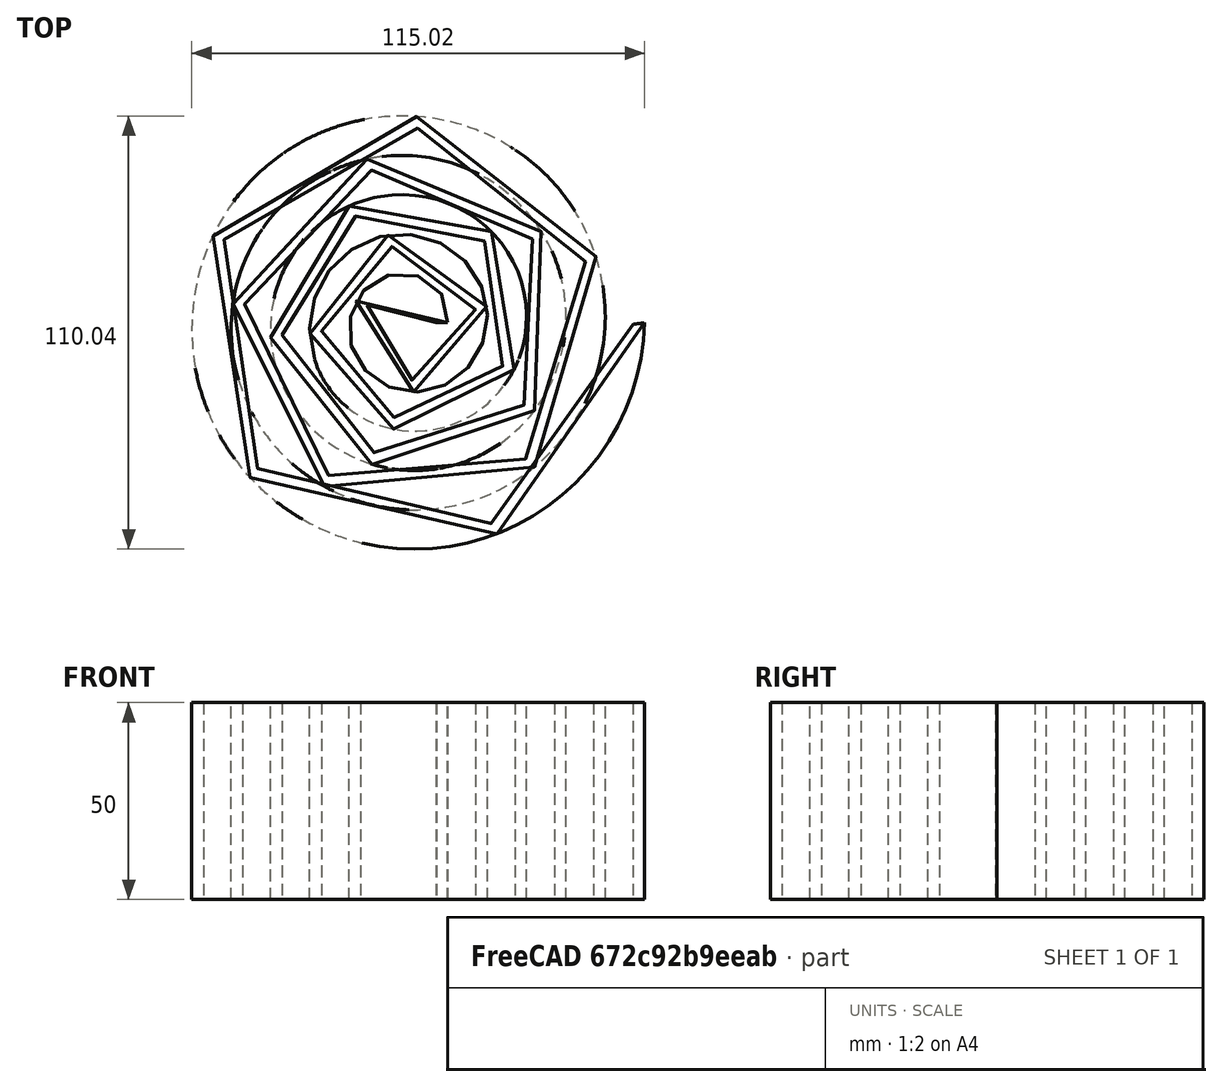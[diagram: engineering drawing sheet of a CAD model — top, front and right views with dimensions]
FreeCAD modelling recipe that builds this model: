
FCSTD DOCUMENT  (FreeCAD 0.17R13247 (Git))
Label: MOLA ESPIRAL
License: All rights reserved
LicenseURL: http://en.wikipedia.org/wiki/All_rights_reserved
objects: Part::Spiral×1, Sketcher::SketchObject×1, PartDesign::Body×1, Part::Sweep×1, Fem::FemSolverObjectPython×1, App::MaterialObjectPython×1, Fem::ConstraintFixed×1, Fem::ConstraintForce×1, Fem::FemMeshShapeNetgenObject×1, Fem::FemMeshObjectPython×1, Fem::FemResultObjectPython×1, Fem::FemAnalysis×1
note: 4 computed .brp shape members not serialized (recipe doc carries the construction recipe); baked Part::Feature solids carry a one-line shape summary decoded from their .brp

FEATURE [Part::Spiral] Spiral
  AttacherType = Attacher::AttachEngine3D
  Growth = 10
  Radius = 10
  Rotations = 5
FEATURE [Sketcher::SketchObject] Sketch
  AttachmentOffset = pos=(10,0,0) rot=(0,0,1;0rad)
  MapMode = 5
  Placement = pos=(10,0,0) rot=(1,0,0;1.5708rad)
  Support = -> [XZ_Plane]
  sketch-geometry (4):
    g0: LineSegment StartX=-3 StartY=0 StartZ=0 EndX=0 EndY=0 EndZ=0
    g1: LineSegment StartX=0 StartY=0 StartZ=0 EndX=0 EndY=50 EndZ=0
    g2: LineSegment StartX=0 StartY=50 StartZ=0 EndX=-3 EndY=50 EndZ=0
    g3: LineSegment StartX=-3 StartY=50 StartZ=0 EndX=-3 EndY=0 EndZ=0
  constraints (12):
    c: Coincident(g0,g1)
    c: Coincident(g1,g2)
    c: Coincident(g2,g3)
    c: Coincident(g3,g0)
    c: Horizontal(g0)
    c: Horizontal(g2)
    c: Vertical(g1)
    c: Vertical(g3)
    c: PointOnObject(g0,g-1)
    c: DistanceX(g2,g2) = 3
    c: DistanceY(g3,g3) = 50
    c: Coincident(g0,g-1)
FEATURE [PartDesign::Body] Body
  Group = -> [Sketch]
  Origin = -> Origin
FEATURE [Part::Sweep] Sweep
  Frenet = true
  Sections = -> [Sketch]
  Solid = true
  Spine = -> Spiral [Edge1]
  Transition = 1
FEATURE [Fem::FemSolverObjectPython] CalculiXccxTools  # FEM object (typed FeaturePython)
  AnalysisType = 0
  BeamShellResultOutput3D = false
  EigenmodeHighLimit = 1000000
  EigenmodeLowLimit = 0
  EigenmodesCount = 10
  GeometricalNonlinearity = 0
  IterationsControlParameterCutb = 0.25,0.5,0.75,0.85,,,1.5,
  IterationsControlParameterIter = 4,8,9,200,10,400,,200,,
  IterationsControlParameterTimeUse = false
  IterationsThermoMechMaximum = 2000
  IterationsUserDefinedIncrementations = false
  IterationsUserDefinedTimeStepLength = false
  MaterialNonlinearity = 0
  MatrixSolverType = 0
  SplitInputWriter = false
  ThermoMechSteadyState = true
  TimeEnd = 1
  TimeInitialStep = 0.01
FEATURE [App::MaterialObjectPython] SolidMaterial  # material (typed FeaturePython)
  Category = 0
  Material = Density=7900.0 kg/m^3,+10 more (map truncated)
FEATURE [Fem::ConstraintFixed] FemConstraintFixed
  NormalDirection = (0,-1,0)
  Normals = (12) [(8.7142e-16,-1,1.60878e-16),(8.7142e-16,-1,1.60878e-16),(8.7142e-16,-1,1.60878e-16),(8.7142e-16,-1,1.60878e-16),(8.7142e-16,-1,1.60878e-16),+7 more]
  Points = (12) [(10,1.01889e-14,50),(8.5,8.88178e-15,50),(7,7.57465e-15,50),(10,7.50762e-15,33.3333),(8.5,6.20049e-15,33.3333),(7,4.89336e-15,33.3333),+6 more]
  References = -> [Sweep]
FEATURE [Fem::ConstraintForce] FemConstraintForce
  DirectionVector = (0.130934,-0.991391,0)
  Force = 500
  NormalDirection = (-0.130934,0.991391,0)
  Points = (12) [(60,1.01114e-13,50),(58.5129,-0.196402,50),(57.0258,-0.392803,50),(60,9.58678e-14,33.3333),(58.5129,-0.196402,33.3333),(57.0258,-0.392803,33.3333),+6 more]
  References = -> [Sweep]
  Reversed = true
FEATURE [Fem::FemMeshShapeNetgenObject] FEMMeshNetgen
  Fineness = 2
  GrowthRate = 0.3
  MaxSize = 1000
  NbSegsPerEdge = 1
  NbSegsPerRadius = 2
  Optimize = true
  SecondOrder = true
  Shape = -> Sweep
FEATURE [Fem::FemMeshObjectPython] Result_mesh  # FEM object (typed FeaturePython)
FEATURE [Fem::FemResultObjectPython] CalculiX_static_results  # FEM object (typed FeaturePython)
  DisplacementLengths = [95.6278,0,99.6116,0,99.6133,0,95.6295,0,99.6135,99.6136,99.6136,99.6136,99.6136,99.6136,99.6135,99.6134,99.6132,99.613,99.6128,99.6125,99.6123,99.6119,95.628,95.6284,95.6286,95.629,95.6293,95.6295,95.6296,95.6297,95.6298,95.6299,95.6299,+34631 more]
  DisplacementVectors = (34664) [(5.25992,-95.483,0.00162099),(0,0,0),(5.78301,-99.4436,0.00213389),(0,0,0),(5.78322,-99.4453,0.00214639),(0,0,0),(5.26012,-95.4847,0.00265733),+34657 more]
  Eigenmode = 0
  EigenmodeFrequency = 0
  MaxShear = [1.5232,131.434,2.14538,131.551,2.02151,133.247,1.59063,131.51,2.52073,2.57269,2.01117,1.96978,1.98595,2.01184,2.0737,2.08081,1.96987,1.96919,1.97016,1.9875,2.59354,2.73142,1.32256,2.23779,2.87844,3.12194,3.14429,3.05931,2.97102,2.93948,+34634 more]
  Mesh = -> Result_mesh
  NodeNumbers = [1,2,3,4,5,6,7,8,9,10,11,12,13,14,15,16,17,18,19,20,21,22,23,24,25,26,27,28,29,30,31,32,33,34,35,36,37,38,39,40,41,42,43,44,45,46,47,48,49,50,51,52,53,54,55,56,57,58,59,60,61,62,63,64,65,66,67,68,69,+34595 more]
  PrincipalMax = [0.217943,317.413,0.757568,-96.4885,0.431398,-98.6231,0.403351,303.551,1.36001,1.41108,0.275748,0.139135,0.110137,0.10331,0.0724254,0.0932734,0.142507,0.157291,0.152781,0.201862,1.47748,1.71238,0.245195,0.253772,0.267701,0.246132,0.205784,+34637 more]
  PrincipalMed = [-0.278267,143.124,0.273865,-206.17,0.0330873,-139.057,-0.488877,122.059,0.156556,0.152449,0.107451,-1.27502,-2.57569,-3.50566,-3.96463,-3.87972,-3.57112,-2.71767,-1.47926,0.0467738,0.168385,0.0941634,-1.95613,-2.45585,-2.29878,-2.25784,+34638 more]
  PrincipalMin = [-2.82846,54.5454,-3.53319,-359.591,-3.61163,-365.117,-2.77791,40.5321,-3.68146,-3.7343,-3.74659,-3.80042,-3.86177,-3.92037,-4.07498,-4.06835,-3.79723,-3.78109,-3.78754,-3.77315,-3.7096,-3.75046,-2.39993,-4.22181,-5.48918,-5.99774,-6.08279,+34637 more]
  ResultType = Fem::FemResultMechanical
  Stats = [-70.3444,-4.14304,51.4664,-99.4455,-8.52095,46.4167,-0.00976382,0.00108539,0.0129451,0,31.4615,99.6136,1.22366,251.741,847.322,-161.266,129.045,859.35,-247.167,1.93361,257.261,-846.668,-138.55,151.556,0.686458,133.797,426.59,0,0,0,0,0,0,0,+5 more]
  StrainVectors = (34664) [(4.62368e-06,-1.28009e-05,2.39969e-06),(-0.000148791,0.00117896,-2.39959e-10),(5.50624e-06,-1.88316e-05,8.32186e-06),+34661 more]
  StressValues = [2.8311,231.648,4.07052,228.901,3.85932,248.754,2.8422,233.201,4.56043,4.64574,3.94089,3.4567,3.51025,3.83319,4.09335,4.07059,3.83169,3.52896,3.42913,3.89978,4.67217,4.86017,2.45351,3.90458,4.99535,5.44255,5.48411,5.33126,5.17539,5.12945,+34634 more]
  StressVectors = (34664) [(0.0446939,-2.63602,-0.297459),(95.9743,300.243,118.865),(0.269783,-3.4745,0.702956),(-151.496,-357.927,-152.827),(0.17492,-3.57748,0.25542),+34659 more]
  Time = 0
FEATURE [Fem::FemAnalysis] Analysis
  Group = -> [CalculiXccxTools,SolidMaterial,FemConstraintFixed,FemConstraintForce,FEMMeshNetgen,CalculiX_static_results]
